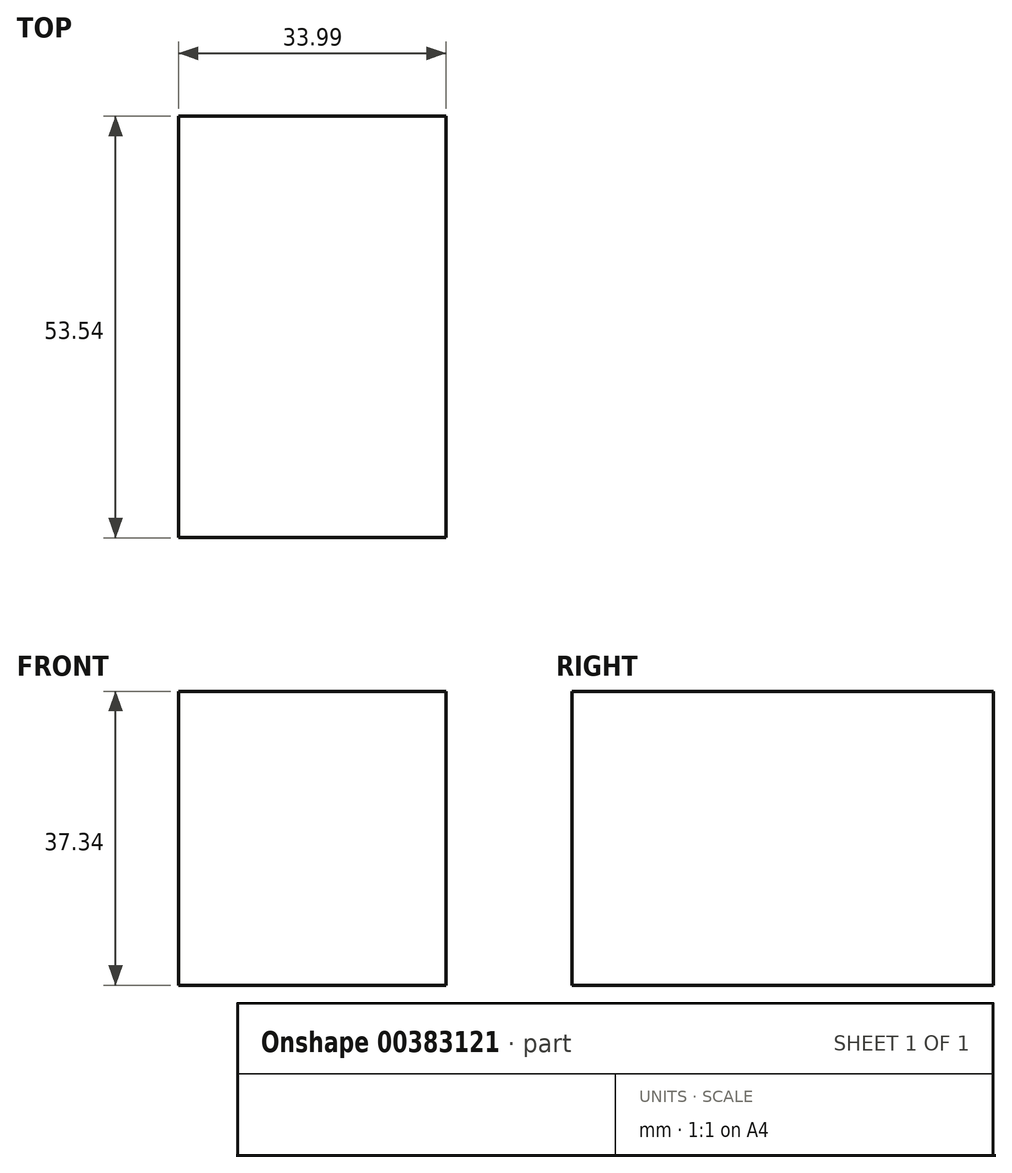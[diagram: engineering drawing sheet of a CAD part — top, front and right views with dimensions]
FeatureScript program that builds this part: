
annotation { "Feature Type Name" : "Feature", "Feature Type Description" : "" }
export const myFeature = defineFeature(function(context is Context, id is Id, definition is map)
    precondition{}
    {
        {
            var Q0;
            Q0=qCreatedBy(makeId("Top.planeOp"),FACE);
            var sketch = newSketch(context, id + "F0", { "sketchPlane" : qUnion([Q0])});
            skLineSegment(sketch, "E0.bottom", {"start": v(-111.52, -53.54) * mm, "end": v(-77.53, -53.54) * mm});
            skLineSegment(sketch, "E0.top", {"start": v(-111.52, 0) * mm, "end": v(-77.53, 0) * mm});
            skLineSegment(sketch, "E0.left", {"start": v(-111.52, -53.54) * mm, "end": v(-111.52, 0) * mm});
            skLineSegment(sketch, "E0.right", {"start": v(-77.53, -53.54) * mm, "end": v(-77.53, 0) * mm});
            skSolve(sketch);
        }
        {
            var Q0;
            Q0=makeQuery(id+"F0.imprint","IMPRINT",FACE,{"disambiguationData":[TD([[makeQuery(id+"F0.imprint","IMPRINT",EDGE,{"derivedFrom":sQuery(id+"F0.wireOp",EDGE,"E0.bottom")}),1.0]])]});
            extrude(context, id + "F1", {"entities" : qUnion([Q0]), "depth" : 37.34 * mm});
        }
    });
